# Revit family: Basin-Above Counter-Caroma Cube 500
name_source: partatom
category: Plumbing Fixtures
revit_build: Autodesk Revit 2014 (Build: 20131024_2115(x64)
units: mm (PartAtom-declared; Revit-internal decimal feet)

## types (1)
- Cube 500 Above Counter
    Assembly Code = D2010310
    CW Connection = No
    Cost = 0 $
    Default Elevation = 0 mm  [stored 0 ft]
    Depth_ANZRS = 150 mm
    Description = Caroma Cube 500 Above Counter Basin
    HW Connection = No
    Keynote = WB
    Length_ANZRS = 500 mm  [stored 1.64042 ft]
    Manufacturer = GWA Bathrooms & Kitchens
    Material_ANZRS = Porcelain-White-Caroma
    Model = 683400W
    ModifiedIssue_ANZRS = 20140916 $
    Type Comments = Overflow not available, White plastic flush fitting uni-plug and waste included
    URL = http://www.caroma.com.au
    Vent Connection = No
    WFU = 2
    Waste = Metal-Chrome-Caroma
    Waste Connection = Yes
    WasteOutlet_ANZRS = 0
    Width_ANZRS = 320 mm  [stored 1.04987 ft]

note: [stored X ft] marks values corroborated as IEEE doubles in the binary element streams (Revit-internal decimal feet)

## geometry (parser evidence)
native form markers: Blend x12, Sweep x1
no freeform markers — native parametric forms only
